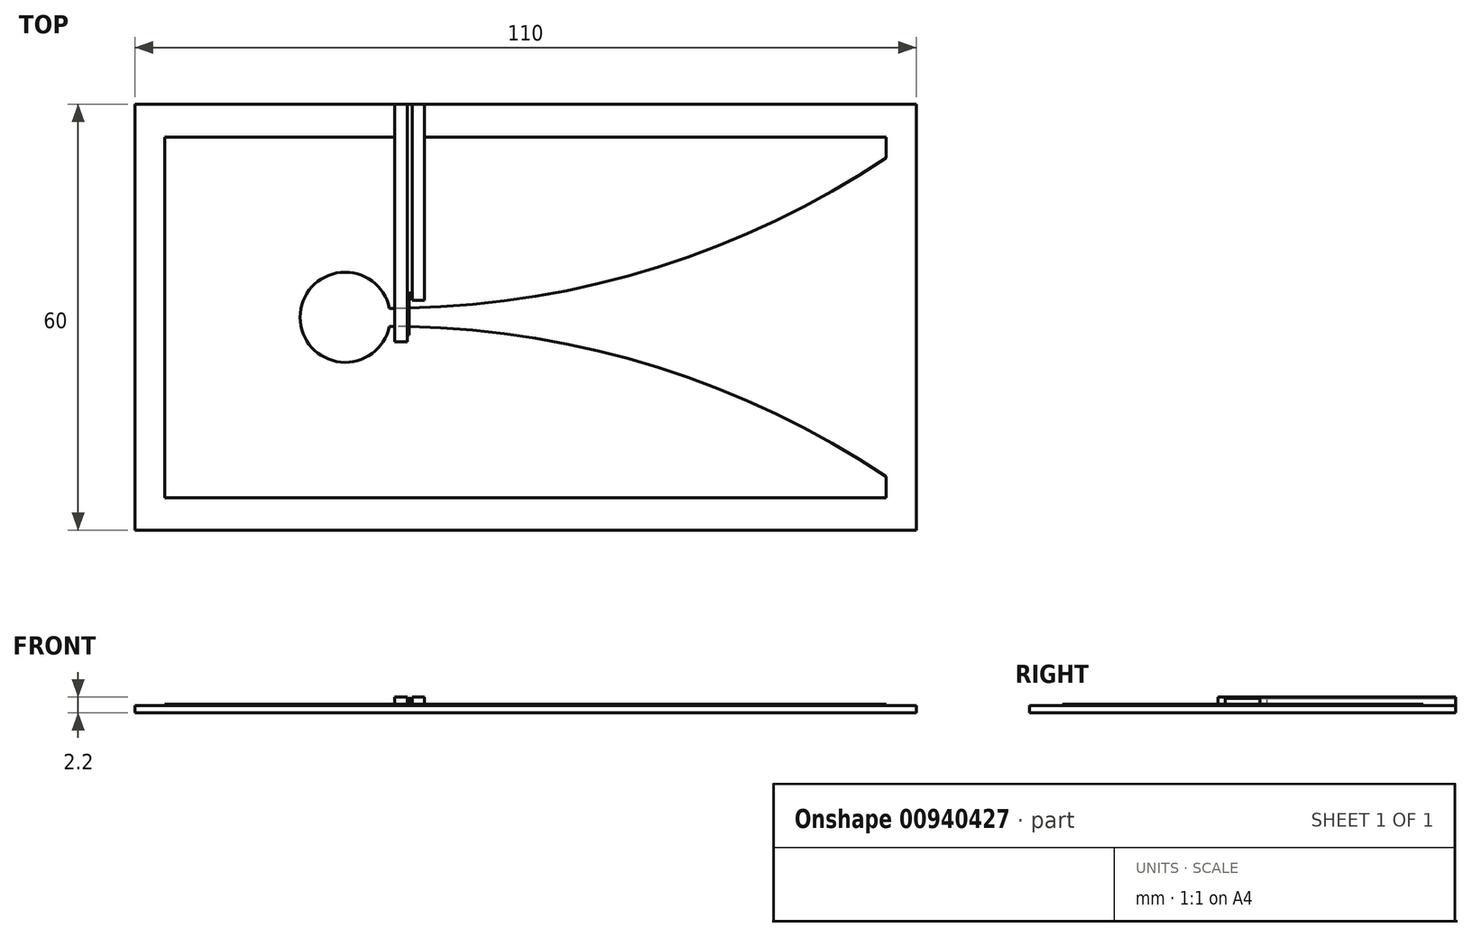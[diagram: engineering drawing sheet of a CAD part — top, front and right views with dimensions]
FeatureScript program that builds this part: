
annotation { "Feature Type Name" : "Feature", "Feature Type Description" : "" }
export const myFeature = defineFeature(function(context is Context, id is Id, definition is map)
    precondition{}
    {
        {
            var Q0;
            Q0=qCreatedBy(makeId("Top.planeOp"),FACE);
            var sketch = newSketch(context, id + "F0", { "sketchPlane" : qUnion([Q0])});
            skLineSegment(sketch, "E0.bottom", {"start": v(50.8, -25.4) * mm, "end": v(-50.8, -25.4) * mm});
            skLineSegment(sketch, "E0.top", {"start": v(50.8, 25.4) * mm, "end": v(-50.8, 25.4) * mm});
            skLineSegment(sketch, "E0.left", {"start": v(50.8, -25.4) * mm, "end": v(50.8, -22.46) * mm});
            skLineSegment(sketch, "E0.right", {"start": v(-50.8, -25.4) * mm, "end": v(-50.8, 25.4) * mm});
            skPoint(sketch, "E0.middle", {"position": v(0, 0) * mm});
            skLineSegment(sketch, "E1", {"start": v(-50.8, 0) * mm, "end": v(-31.75, 0) * mm});
            skArc(sketch, "E2", {"start": v(-19.18, 1.27) * mm, "mid": v(-31.75, 0) * mm, "end": v(-19.18, -1.27) * mm});
            skArc(sketch, "E3", {"start": v(50.8, -22.46) * mm, "mid": v(17.39, -6.66) * mm, "end": v(-19.18, -1.27) * mm});
            skLineSegment(sketch, "E4.trimOffspring", {"start": v(50.8, 22.46) * mm, "end": v(50.8, 25.4) * mm});
            skArc(sketch, "E5.trimOffspring", {"start": v(-19.18, 1.27) * mm, "mid": v(17.39, 6.66) * mm, "end": v(50.8, 22.46) * mm});
            skSolve(sketch);
        }
        {
            var Q0;
            {var subQ2=sQuery(id+"F0.wireOp",EDGE,"E0.top");Q0=makeQuery(id+"F0.imprint","IMPRINT",FACE,{"disambiguationData":[TD([[makeQuery(id+"F0.imprint","IMPRINT",EDGE,{"derivedFrom":subQ2}),1.0]])]});}
            var Q1;
            {var subQ1=sQuery(id+"F0.wireOp",EDGE,"E0.bottom");Q1=makeQuery(id+"F0.imprint","IMPRINT",FACE,{"disambiguationData":[TD([[makeQuery(id+"F0.imprint","IMPRINT",EDGE,{"derivedFrom":subQ1}),-1.0]])]});}
            extrude(context, id + "F1", {"entities" : qUnion([Q0, Q1]), "depth" : .2 * mm, "offsetDistance" : 25 * mm});
        }
        {
            var Q0;
            Q0=makeQuery(id+"F1.opExtrude","CAP_FACE",FACE,{"disambiguationData":[OSD([sQuery(id+"F0.wireOp",EDGE,"E0.bottom"),sQuery(id+"F0.wireOp",EDGE,"E0.top"),sQuery(id+"F0.wireOp",EDGE,"E0.left"),sQuery(id+"F0.wireOp",EDGE,"E0.right"),sQuery(id+"F0.wireOp",EDGE,"E2"),sQuery(id+"F0.wireOp",EDGE,"E3"),sQuery(id+"F0.wireOp",EDGE,"E4.trimOffspring"),sQuery(id+"F0.wireOp",EDGE,"E5.trimOffspring")])],"isStart":true});
            var sketch = newSketch(context, id + "F2", { "sketchPlane" : qUnion([Q0])});
            skLineSegment(sketch, "E6.bottom", {"start": v(55, 30) * mm, "end": v(-55, 30) * mm});
            skLineSegment(sketch, "E6.top", {"start": v(55, -30) * mm, "end": v(-55, -30) * mm});
            skLineSegment(sketch, "E6.left", {"start": v(55, 30) * mm, "end": v(55, -30) * mm});
            skLineSegment(sketch, "E6.right", {"start": v(-55, 30) * mm, "end": v(-55, -30) * mm});
            skPoint(sketch, "E6.middle", {"position": v(0, 0) * mm});
            skSolve(sketch);
        }
        {
            var Q0;
            Q0=makeQuery(id+"F2.imprint","IMPRINT",FACE,{"disambiguationData":[TD([[makeQuery(id+"F2.imprint","IMPRINT",EDGE,{"derivedFrom":sQuery(id+"F2.wireOp",EDGE,"E6.bottom")}),1.0]])]});
            var Q1;
            Q1=makeQuery(id+"F2.imprint","IMPRINT",FACE,{"disambiguationData":[TD([[makeQuery(id+"F2.imprint","IMPRINT",EDGE,{"derivedFrom":makeQuery(id+"F1.opExtrude","CAP_EDGE",EDGE,{"disambiguationData":[OSD([sQuery(id+"F0.wireOp",EDGE,"E0.bottom")])],"isStart":true})}),1.0]])]});
            extrude(context, id + "F3", {"entities" : qUnion([Q0, Q1]), "depth" : 1 * mm, "offsetDistance" : 25 * mm});
        }
        {
            var Q0;
            Q0=makeQuery(id+"F1.opExtrude","CAP_FACE",FACE,{"disambiguationData":[OSD([sQuery(id+"F0.wireOp",EDGE,"E0.bottom"),sQuery(id+"F0.wireOp",EDGE,"E0.top"),sQuery(id+"F0.wireOp",EDGE,"E0.left"),sQuery(id+"F0.wireOp",EDGE,"E0.right"),sQuery(id+"F0.wireOp",EDGE,"E2"),sQuery(id+"F0.wireOp",EDGE,"E3"),sQuery(id+"F0.wireOp",EDGE,"E4.trimOffspring"),sQuery(id+"F0.wireOp",EDGE,"E5.trimOffspring")])],"isStart":false});
            var sketch = newSketch(context, id + "F4", { "sketchPlane" : qUnion([Q0])});
            skLineSegment(sketch, "E7.bottom", {"start": v(-18.42, 3.4) * mm, "end": v(-14.24, 3.4) * mm});
            skLineSegment(sketch, "E7.top", {"start": v(-18.42, 25.4) * mm, "end": v(-14.24, 25.4) * mm});
            skLineSegment(sketch, "E7.left", {"start": v(-18.42, 3.4) * mm, "end": v(-18.42, 25.4) * mm});
            skLineSegment(sketch, "E7.right", {"start": v(-14.24, 3.4) * mm, "end": v(-14.24, 25.4) * mm});
            skLineSegment(sketch, "E8.bottom", {"start": v(-18.42, 3.4) * mm, "end": v(-16.42, 3.4) * mm});
            skLineSegment(sketch, "E8.top", {"start": v(-18.42, -2.47) * mm, "end": v(-16.42, -2.47) * mm});
            skLineSegment(sketch, "E8.left", {"start": v(-18.42, 3.4) * mm, "end": v(-18.42, -2.47) * mm});
            skLineSegment(sketch, "E8.right", {"start": v(-16.42, 3.4) * mm, "end": v(-16.42, -2.47) * mm});
            skSolve(sketch);
        }
        {
            var Q0;
            {var subQ0=sQuery(id+"F4.wireOp",EDGE,"E8.top");Q0=makeQuery(id+"F4.imprint","IMPRINT",FACE,{"disambiguationData":[TD([[makeQuery(id+"F4.imprint","IMPRINT",EDGE,{"derivedFrom":subQ0}),1.0]])]});}
            var Q1;
            {var subQ0=sQuery(id+"F4.wireOp",EDGE,"E8.left");var subQ1=makeQuery(id+"F1.opExtrude","CAP_EDGE",EDGE,{"disambiguationData":[OSD([sQuery(id+"F0.wireOp",EDGE,"E5.trimOffspring")])],"isStart":false});var subQ2=makeQuery(id+"F4.imprint","INTERSECT",VERTEX,{"derivedFrom":[subQ1,subQ0]});Q1=makeQuery(id+"F4.imprint","IMPRINT",FACE,{"disambiguationData":[TD([[makeQuery(id+"F4.imprint","IMPRINT",EDGE,{"disambiguationData":[TD([[subQ2,-1.0]])],"derivedFrom":subQ0}),1.0]])]});}
            var Q2;
            {var subQ0=sQuery(id+"F4.wireOp",EDGE,"E8.right");var subQ1=sQuery(id+"F4.wireOp",EDGE,"E7.bottom");var subQ2=makeQuery(id+"F4.imprint","INTERSECT",VERTEX,{"derivedFrom":[subQ1,subQ0]});Q2=makeQuery(id+"F4.imprint","IMPRINT",FACE,{"disambiguationData":[TD([[makeQuery(id+"F4.imprint","IMPRINT",EDGE,{"disambiguationData":[TD([[subQ2,-1.0]])],"derivedFrom":subQ0}),-1.0]])]});}
            var Q3;
            Q3=makeQuery(id+"F4.imprint","IMPRINT",FACE,{"disambiguationData":[TD([[makeQuery(id+"F4.imprint","IMPRINT",EDGE,{"derivedFrom":sQuery(id+"F4.wireOp",EDGE,"E7.top")}),1.0]])]});
            extrude(context, id + "F5", {"entities" : qUnion([Q0, Q1, Q2, Q3]), "operationType" : NewBodyOperationType.ADD, "depth" : .8 * mm, "offsetDistance" : 25 * mm});
        }
        {
            var Q0;
            Q0=makeQuery(id+"F3.opExtrude","CAP_FACE",FACE,{"disambiguationData":[OSD([sQuery(id+"F2.wireOp",EDGE,"E6.bottom"),sQuery(id+"F2.wireOp",EDGE,"E6.top"),sQuery(id+"F2.wireOp",EDGE,"E6.left"),sQuery(id+"F2.wireOp",EDGE,"E6.right")])],"isStart":true});
            var sketch = newSketch(context, id + "F6", { "sketchPlane" : qUnion([Q0])});
            skPoint(sketch, "E9.0", {"position": v(-18.42, 25.4) * mm});
            skPoint(sketch, "E10.0", {"position": v(-14.24, 25.4) * mm});
            skLineSegment(sketch, "E11.0", {"start": v(55, 30) * mm, "end": v(-55, 30) * mm});
            skLineSegment(sketch, "E12.bottom", {"start": v(-18.42, 25.4) * mm, "end": v(-14.24, 25.4) * mm});
            skLineSegment(sketch, "E12.top", {"start": v(-18.42, 30) * mm, "end": v(-14.24, 30) * mm});
            skLineSegment(sketch, "E12.left", {"start": v(-18.42, 25.4) * mm, "end": v(-18.42, 30) * mm});
            skLineSegment(sketch, "E12.right", {"start": v(-14.24, 25.4) * mm, "end": v(-14.24, 30) * mm});
            skSolve(sketch);
        }
        {
            var Q0;
            Q0=makeQuery(id+"F6.imprint","IMPRINT",FACE,{"disambiguationData":[TD([[makeQuery(id+"F6.imprint","IMPRINT",EDGE,{"derivedFrom":sQuery(id+"F6.wireOp",EDGE,"E12.bottom")}),1.0]])]});
            extrude(context, id + "F7", {"entities" : qUnion([Q0]), "operationType" : NewBodyOperationType.ADD, "depth" : 1 * mm, "offsetDistance" : 25 * mm});
        }
        {
            var Q0;
            Q0=makeQuery(id+"F7.boolean.opBoolean","MERGE",FACE,{"derivedFrom":[makeQuery(id+"F5.opExtrude","CAP_FACE",FACE,{"disambiguationData":[OSD([sQuery(id+"F4.wireOp",EDGE,"E7.bottom"),sQuery(id+"F4.wireOp",EDGE,"E7.top"),sQuery(id+"F4.wireOp",EDGE,"E7.left"),sQuery(id+"F4.wireOp",EDGE,"E7.right"),sQuery(id+"F4.wireOp",EDGE,"E8.top"),sQuery(id+"F4.wireOp",EDGE,"E8.left"),sQuery(id+"F4.wireOp",EDGE,"E8.right")])],"isStart":false}),makeQuery(id+"F7.opExtrude","CAP_FACE",FACE,{"disambiguationData":[OSD([sQuery(id+"F6.wireOp",EDGE,"E11.0"),sQuery(id+"F6.wireOp",EDGE,"E12.bottom"),sQuery(id+"F6.wireOp",EDGE,"E12.left"),sQuery(id+"F6.wireOp",EDGE,"E12.right")])],"isStart":false})]});
            var sketch = newSketch(context, id + "F8", { "sketchPlane" : qUnion([Q0])});
            skPoint(sketch, "E13.oppositeSnap0", {"position": v(-15.99, 30) * mm});
            skPoint(sketch, "E13.oppositeSnap1", {"position": v(-16.67, -2.47) * mm});
            skLineSegment(sketch, "E13.bottom", {"start": v(-18.42, -2.47) * mm, "end": v(-16.67, -2.47) * mm});
            skLineSegment(sketch, "E13.top", {"start": v(-18.42, 30) * mm, "end": v(-16.67, 30) * mm});
            skLineSegment(sketch, "E13.left", {"start": v(-18.42, -2.47) * mm, "end": v(-18.42, 30) * mm});
            skLineSegment(sketch, "E13.right", {"start": v(-16.67, -2.47) * mm, "end": v(-16.67, 30) * mm});
            skLineSegment(sketch, "E14.bottom", {"start": v(-14.24, 3.4) * mm, "end": v(-15.99, 3.4) * mm});
            skLineSegment(sketch, "E14.top", {"start": v(-14.24, 30) * mm, "end": v(-15.99, 30) * mm});
            skLineSegment(sketch, "E14.left", {"start": v(-14.24, 3.4) * mm, "end": v(-14.24, 30) * mm});
            skLineSegment(sketch, "E14.right", {"start": v(-15.99, 3.4) * mm, "end": v(-15.99, 30) * mm});
            skSolve(sketch);
        }
        {
            var Q0;
            Q0=makeQuery(id+"F8.imprint","IMPRINT",FACE,{"disambiguationData":[TD([[makeQuery(id+"F8.imprint","IMPRINT",EDGE,{"derivedFrom":sQuery(id+"F8.wireOp",EDGE,"E13.bottom")}),1.0]])]});
            var Q1;
            Q1=makeQuery(id+"F8.imprint","IMPRINT",FACE,{"disambiguationData":[TD([[makeQuery(id+"F8.imprint","IMPRINT",EDGE,{"derivedFrom":sQuery(id+"F8.wireOp",EDGE,"E14.bottom")}),1.0]])]});
            extrude(context, id + "F9", {"entities" : qUnion([Q0, Q1]), "operationType" : NewBodyOperationType.ADD, "depth" : .2 * mm, "offsetDistance" : 25 * mm});
        }
        {
            var Q0;
            Q0=makeQuery(id+"F1.opExtrude","CAP_FACE",FACE,{"disambiguationData":[OSD([sQuery(id+"F0.wireOp",EDGE,"E0.bottom"),sQuery(id+"F0.wireOp",EDGE,"E0.top"),sQuery(id+"F0.wireOp",EDGE,"E0.left"),sQuery(id+"F0.wireOp",EDGE,"E0.right"),sQuery(id+"F0.wireOp",EDGE,"E2"),sQuery(id+"F0.wireOp",EDGE,"E3"),sQuery(id+"F0.wireOp",EDGE,"E4.trimOffspring"),sQuery(id+"F0.wireOp",EDGE,"E5.trimOffspring")])],"isStart":false});
            var sketch = newSketch(context, id + "F10", { "sketchPlane" : qUnion([Q0])});
            skPoint(sketch, "E15.0", {"position": v(-15.99, 3.4) * mm});
            skPoint(sketch, "E16.0", {"position": v(-14.24, 3.4) * mm});
            skPoint(sketch, "E17.0", {"position": v(-18.42, -2.47) * mm});
            skPoint(sketch, "E18.0", {"position": v(-16.67, -2.47) * mm});
            skLineSegment(sketch, "E19.bottom", {"start": v(-18.42, -2.47) * mm, "end": v(-16.67, -2.47) * mm});
            skLineSegment(sketch, "E19.top", {"start": v(-18.42, -3.47) * mm, "end": v(-16.67, -3.47) * mm});
            skLineSegment(sketch, "E19.left", {"start": v(-18.42, -2.47) * mm, "end": v(-18.42, -3.47) * mm});
            skLineSegment(sketch, "E19.right", {"start": v(-16.67, -2.47) * mm, "end": v(-16.67, -3.47) * mm});
            skLineSegment(sketch, "E20.bottom", {"start": v(-15.99, 3.4) * mm, "end": v(-14.24, 3.4) * mm});
            skLineSegment(sketch, "E20.top", {"start": v(-15.99, 2.4) * mm, "end": v(-14.24, 2.4) * mm});
            skLineSegment(sketch, "E20.left", {"start": v(-15.99, 3.4) * mm, "end": v(-15.99, 2.4) * mm});
            skLineSegment(sketch, "E20.right", {"start": v(-14.24, 3.4) * mm, "end": v(-14.24, 2.4) * mm});
            skSolve(sketch);
        }
        {
            var Q0;
            Q0=makeQuery(id+"F10.imprint","IMPRINT",FACE,{"disambiguationData":[TD([[makeQuery(id+"F10.imprint","IMPRINT",EDGE,{"derivedFrom":sQuery(id+"F10.wireOp",EDGE,"E19.bottom")}),-1.0]])]});
            var Q1;
            Q1=makeQuery(id+"F10.imprint","IMPRINT",FACE,{"disambiguationData":[TD([[makeQuery(id+"F10.imprint","IMPRINT",EDGE,{"derivedFrom":sQuery(id+"F10.wireOp",EDGE,"E20.bottom")}),-1.0]])]});
            extrude(context, id + "F11", {"entities" : qUnion([Q0, Q1]), "operationType" : NewBodyOperationType.ADD, "depth" : 1 * mm, "offsetDistance" : 25 * mm});
        }
    });
